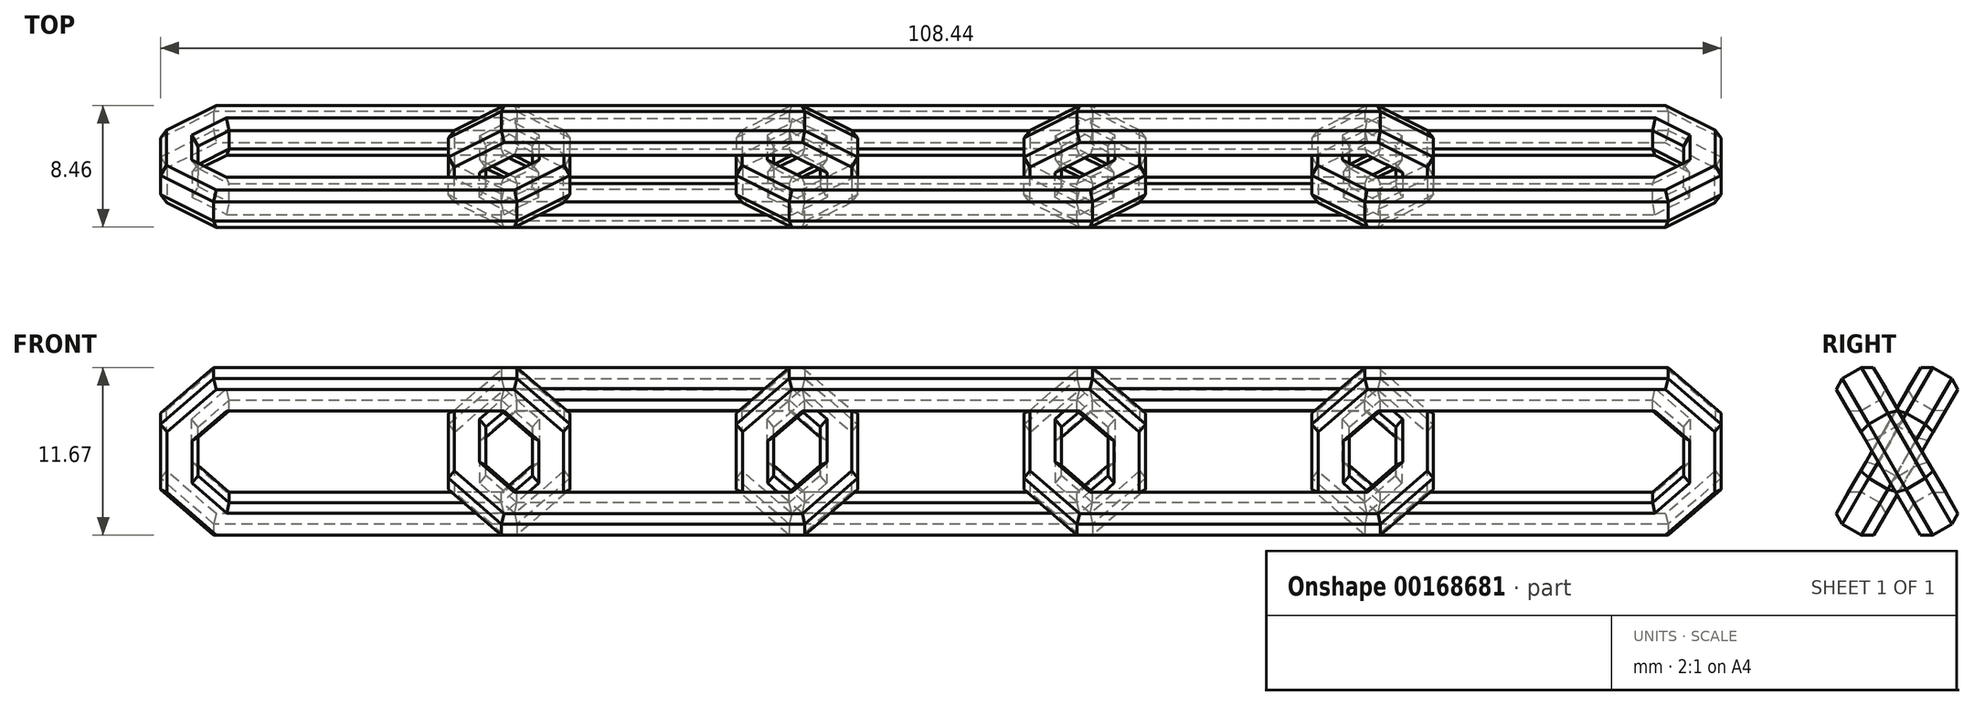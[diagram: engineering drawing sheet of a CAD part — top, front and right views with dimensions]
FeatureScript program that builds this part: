
annotation { "Feature Type Name" : "Feature", "Feature Type Description" : "" }
export const myFeature = defineFeature(function(context is Context, id is Id, definition is map)
    precondition{}
    {
        {
            var Q0;
            Q0=qCreatedBy(makeId("Front.planeOp"),FACE);
            var sketch = newSketch(context, id + "F0", { "sketchPlane" : qUnion([Q0])});
            skCircle(sketch, "E0.cCircle", {"center": v(-6.08, 0) * mm, "radius": 1.5 * mm, "construction": true});
            skLineSegment(sketch, "E0.1", {"start": v(-5.23, -1.51) * mm, "end": v(-6.96, -1.49) * mm});
            skLineSegment(sketch, "E0.4", {"start": v(-6.93, 1.51) * mm, "end": v(-5.2, 1.49) * mm});
            skPoint(sketch, "E0.0.midPoint", {"position": v(-4.79, -0.77) * mm});
            skLineSegment(sketch, "E1", {"start": v(-5.23, -1.51) * mm, "end": v(-4.79, -0.77) * mm});
            skLineSegment(sketch, "E2", {"start": v(-4.79, 0.77) * mm, "end": v(-5.2, 1.49) * mm});
            skLineSegment(sketch, "E3", {"start": v(-4.79, 0.77) * mm, "end": v(-4.79, -0.77) * mm});
            skLineSegment(sketch, "E4", {"start": v(-6.96, -1.49) * mm, "end": v(-7.39, -0.73) * mm});
            skLineSegment(sketch, "E5", {"start": v(-7.39, -0.73) * mm, "end": v(-7.39, 0.73) * mm});
            skLineSegment(sketch, "E6", {"start": v(-7.39, 0.73) * mm, "end": v(-6.93, 1.51) * mm});
            skSolve(sketch);
        }
        {
            var Q0;
            Q0=qCreatedBy(makeId("Top.planeOp"),FACE);
            var sketch = newSketch(context, id + "F1", { "sketchPlane" : qUnion([Q0])});
            skLineSegment(sketch, "E7.rect.bottom", {"start": v(-29, -5) * mm, "end": v(-9, -5) * mm});
            skLineSegment(sketch, "E7.rect.top", {"start": v(-29, 5) * mm, "end": v(-9, 5) * mm});
            skLineSegment(sketch, "E7.rect.left", {"start": v(-29, -5) * mm, "end": v(-29, 5) * mm, "construction": true});
            skLineSegment(sketch, "E7.rect.right", {"start": v(-9, -5) * mm, "end": v(-9, 5) * mm, "construction": true});
            skPoint(sketch, "E7.rect.middle", {"position": v(-19, 0) * mm});
            skLineSegment(sketch, "E8", {"start": v(-9, 5) * mm, "end": v(-6.08, 2.07) * mm});
            skLineSegment(sketch, "E9", {"start": v(-6.08, 2.07) * mm, "end": v(-6.08, -2.07) * mm});
            skLineSegment(sketch, "E10", {"start": v(-6.08, -2.07) * mm, "end": v(-9, -5) * mm});
            skLineSegment(sketch, "E11", {"start": v(-29, 5) * mm, "end": v(-31.94, 2.07) * mm});
            skLineSegment(sketch, "E12", {"start": v(-31.94, 2.07) * mm, "end": v(-31.94, -2.07) * mm});
            skLineSegment(sketch, "E13", {"start": v(-31.94, -2.07) * mm, "end": v(-29, -5) * mm});
            skLineSegment(sketch, "E14", {"start": v(-31.94, 0) * mm, "end": v(-6.08, 0) * mm, "construction": true});
            skSolve(sketch);
        }
        {
            var Q0;
            Q0=makeQuery(id+"F0.imprint","IMPRINT",FACE,{"disambiguationData":[TD([[makeQuery(id+"F0.imprint","IMPRINT",EDGE,{"derivedFrom":sQuery(id+"F0.wireOp",EDGE,"E0.1")}),-1.0]])]});
            var Q1;
            Q1=qConstructionFilter(qBodyType(qCreatedBy(id+"F1",EDGE),BodyType.WIRE),ConstructionObject.NO);
            sweep(context, id + "F2", {"profiles" : qUnion([Q0]), "path" : qUnion([Q1])});
        }
        {
            var Q0;
            Q0=makeQuery(id+"F2.opSweep","SWEPT_BODY",BODY,{"disambiguationData":[OSD([sQuery(id+"F0.wireOp",EDGE,"E0.0"),sQuery(id+"F0.wireOp",EDGE,"E0.1"),sQuery(id+"F0.wireOp",EDGE,"E0.2"),sQuery(id+"F0.wireOp",EDGE,"E0.3"),sQuery(id+"F0.wireOp",EDGE,"E0.4"),sQuery(id+"F0.wireOp",EDGE,"E0.5"),sQuery(id+"F1.wireOp",EDGE,"E11")])]});
            var Q1;
            Q1=sQuery(id+"F1.wireOp",EDGE,"E14");
            transform(context, id + "F3", {"entities" : qUnion([Q0]), "transformType" : TransformType.ROTATION, "transformAxis" : qUnion([Q1]), "angle" : 60 * degree, "makeCopy" : false});
        }
        {
            var Q0;
            Q0=makeQuery(id+"F2.opSweep","SWEPT_BODY",BODY,{"disambiguationData":[OSD([sQuery(id+"F0.wireOp",EDGE,"E0.0"),sQuery(id+"F0.wireOp",EDGE,"E0.1"),sQuery(id+"F0.wireOp",EDGE,"E0.2"),sQuery(id+"F0.wireOp",EDGE,"E0.3"),sQuery(id+"F0.wireOp",EDGE,"E0.4"),sQuery(id+"F0.wireOp",EDGE,"E0.5"),sQuery(id+"F1.wireOp",EDGE,"E11")])]});
            var Q1;
            Q1=qCreatedBy(makeId("Front.planeOp"),FACE);
            mirror(context, id + "F4", {"entities" : qUnion([Q0]), "mirrorPlane" : qUnion([Q1])});
        }
        {
            var Q0;
            Q0=makeQuery(id+"F2.opSweep","SWEPT_BODY",BODY,{"disambiguationData":[OSD([sQuery(id+"F0.wireOp",EDGE,"E0.0"),sQuery(id+"F0.wireOp",EDGE,"E0.1"),sQuery(id+"F0.wireOp",EDGE,"E0.2"),sQuery(id+"F0.wireOp",EDGE,"E0.3"),sQuery(id+"F0.wireOp",EDGE,"E0.4"),sQuery(id+"F0.wireOp",EDGE,"E0.5"),sQuery(id+"F1.wireOp",EDGE,"E11")])]});
            transform(context, id + "F5", {"entities" : qUnion([Q0]), "transformType" : TransformType.TRANSLATION_3D, "dx" : 20 * mm, "dy" : 0 * mm, "dz" : 0 * mm, "makeCopy" : false});
        }
        {
            var Q0;
            Q0=makeQuery(id+"F4.opPattern","COPY",BODY,{"derivedFrom":makeQuery(id+"F2.opSweep","SWEPT_BODY",BODY,{"disambiguationData":[OSD([sQuery(id+"F0.wireOp",EDGE,"E0.0"),sQuery(id+"F0.wireOp",EDGE,"E0.1"),sQuery(id+"F0.wireOp",EDGE,"E0.2"),sQuery(id+"F0.wireOp",EDGE,"E0.3"),sQuery(id+"F0.wireOp",EDGE,"E0.4"),sQuery(id+"F0.wireOp",EDGE,"E0.5"),sQuery(id+"F1.wireOp",EDGE,"E11")])]}),"instanceName":"1"});
            var Q1;
            Q1=makeQuery(id+"F2.opSweep","SWEPT_BODY",BODY,{"disambiguationData":[OSD([sQuery(id+"F0.wireOp",EDGE,"E0.0"),sQuery(id+"F0.wireOp",EDGE,"E0.1"),sQuery(id+"F0.wireOp",EDGE,"E0.2"),sQuery(id+"F0.wireOp",EDGE,"E0.3"),sQuery(id+"F0.wireOp",EDGE,"E0.4"),sQuery(id+"F0.wireOp",EDGE,"E0.5"),sQuery(id+"F1.wireOp",EDGE,"E11")])]});
            transform(context, id + "F6", {"entities" : qUnion([Q0, Q1]), "transformType" : TransformType.TRANSLATION_3D, "dx" : 40 * mm, "dy" : 0 * mm, "dz" : 0 * mm, "makeCopy" : true});
        }
        {
            var Q0;
            Q0=makeQuery(id+"F4.opPattern","COPY",BODY,{"derivedFrom":makeQuery(id+"F2.opSweep","SWEPT_BODY",BODY,{"disambiguationData":[OSD([sQuery(id+"F0.wireOp",EDGE,"E0.0"),sQuery(id+"F0.wireOp",EDGE,"E0.1"),sQuery(id+"F0.wireOp",EDGE,"E0.2"),sQuery(id+"F0.wireOp",EDGE,"E0.3"),sQuery(id+"F0.wireOp",EDGE,"E0.4"),sQuery(id+"F0.wireOp",EDGE,"E0.5"),sQuery(id+"F1.wireOp",EDGE,"E11")])]}),"instanceName":"1"});
            transform(context, id + "F7", {"entities" : qUnion([Q0]), "transformType" : TransformType.TRANSLATION_3D, "dx" : 80 * mm, "dy" : 0 * mm, "dz" : 0 * mm, "makeCopy" : true});
        }
    });
